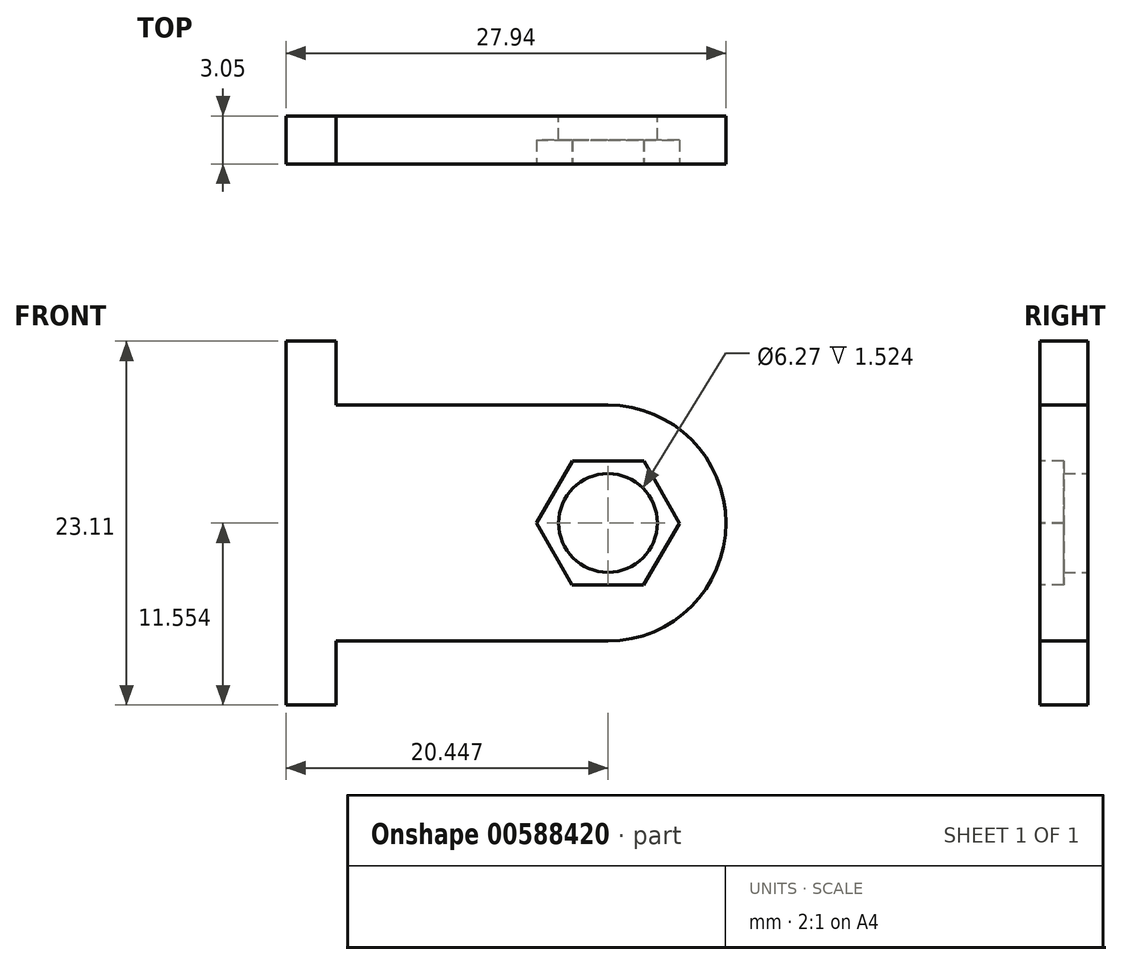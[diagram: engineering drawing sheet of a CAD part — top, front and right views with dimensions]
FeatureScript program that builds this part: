
annotation { "Feature Type Name" : "Feature", "Feature Type Description" : "" }
export const myFeature = defineFeature(function(context is Context, id is Id, definition is map)
    precondition{}
    {
        {
            var Q0;
            Q0=qCreatedBy(makeId("Front.planeOp"),FACE);
            var sketch = newSketch(context, id + "F0", { "sketchPlane" : qUnion([Q0])});
            skLineSegment(sketch, "E0.bottom", {"start": v(-12.7, 0.6) * mm, "end": v(-9.53, 0.6) * mm});
            skLineSegment(sketch, "E0.top", {"start": v(-12.7, -22.52) * mm, "end": v(-9.53, -22.52) * mm});
            skLineSegment(sketch, "E0.left", {"start": v(-12.7, 0.6) * mm, "end": v(-12.7, -22.52) * mm});
            skLineSegment(sketch, "E0.right", {"start": v(-9.53, 0.6) * mm, "end": v(-9.53, -3.47) * mm});
            skLineSegment(sketch, "E1.bottom", {"start": v(-9.53, -3.47) * mm, "end": v(7.74, -3.47) * mm});
            skLineSegment(sketch, "E1.top", {"start": v(-9.53, -18.46) * mm, "end": v(7.74, -18.46) * mm});
            skLineSegment(sketch, "E2.trimOffspring", {"start": v(-9.53, -18.46) * mm, "end": v(-9.53, -22.52) * mm});
            skArc(sketch, "E3", {"start": v(7.74, -18.46) * mm, "mid": v(15.23, -10.97) * mm, "end": v(7.74, -3.47) * mm});
            skCircle(sketch, "E4", {"center": v(7.74, -10.97) * mm, "radius": 3.14 * mm});
            skSolve(sketch);
        }
        {
            var Q0;
            Q0 = qSketchRegion(id + "F0", true);
            extrude(context, id + "F1", {"entities" : qUnion([Q0]), "depth" : 3.05 * mm, "offsetDistance" : 25.4 * mm});
        }
        {
            var Q0;
            Q0=makeQuery(id+"F1.opExtrude","CAP_FACE",FACE,{"disambiguationData":[OSD([sQuery(id+"F0.wireOp",EDGE,"E0.bottom"),sQuery(id+"F0.wireOp",EDGE,"E0.top"),sQuery(id+"F0.wireOp",EDGE,"E0.left"),sQuery(id+"F0.wireOp",EDGE,"E0.right"),sQuery(id+"F0.wireOp",EDGE,"E1.bottom"),sQuery(id+"F0.wireOp",EDGE,"E1.top"),sQuery(id+"F0.wireOp",EDGE,"E2.trimOffspring"),sQuery(id+"F0.wireOp",EDGE,"E3"),sQuery(id+"F0.wireOp",EDGE,"E4")])],"isStart":false});
            var sketch = newSketch(context, id + "F2", { "sketchPlane" : qUnion([Q0])});
            skCircle(sketch, "E5.cCircle", {"center": v(7.74, -10.97) * mm, "radius": 3.94 * mm, "construction": true});
            skLineSegment(sketch, "E5.0", {"start": v(3.2, -10.95) * mm, "end": v(5.48, -7.02) * mm});
            skLineSegment(sketch, "E5.1", {"start": v(5.48, -7.02) * mm, "end": v(10.02, -7.04) * mm});
            skLineSegment(sketch, "E5.2", {"start": v(10.02, -7.04) * mm, "end": v(12.28, -10.98) * mm});
            skLineSegment(sketch, "E5.3", {"start": v(12.28, -10.98) * mm, "end": v(10, -14.91) * mm});
            skLineSegment(sketch, "E5.4", {"start": v(10, -14.91) * mm, "end": v(5.45, -14.9) * mm});
            skLineSegment(sketch, "E5.5", {"start": v(5.45, -14.9) * mm, "end": v(3.2, -10.95) * mm});
            skPoint(sketch, "E5.0.midPoint", {"position": v(4.33, -8.99) * mm});
            skSolve(sketch);
        }
        {
            var Q0;
            Q0 = qSketchRegion(id + "F2", true);
            extrude(context, id + "F3", {"entities" : qUnion([Q0]), "operationType" : NewBodyOperationType.REMOVE, "oppositeDirection" : true, "depth" : 1.52 * mm, "offsetDistance" : 25.4 * mm});
        }
    });
